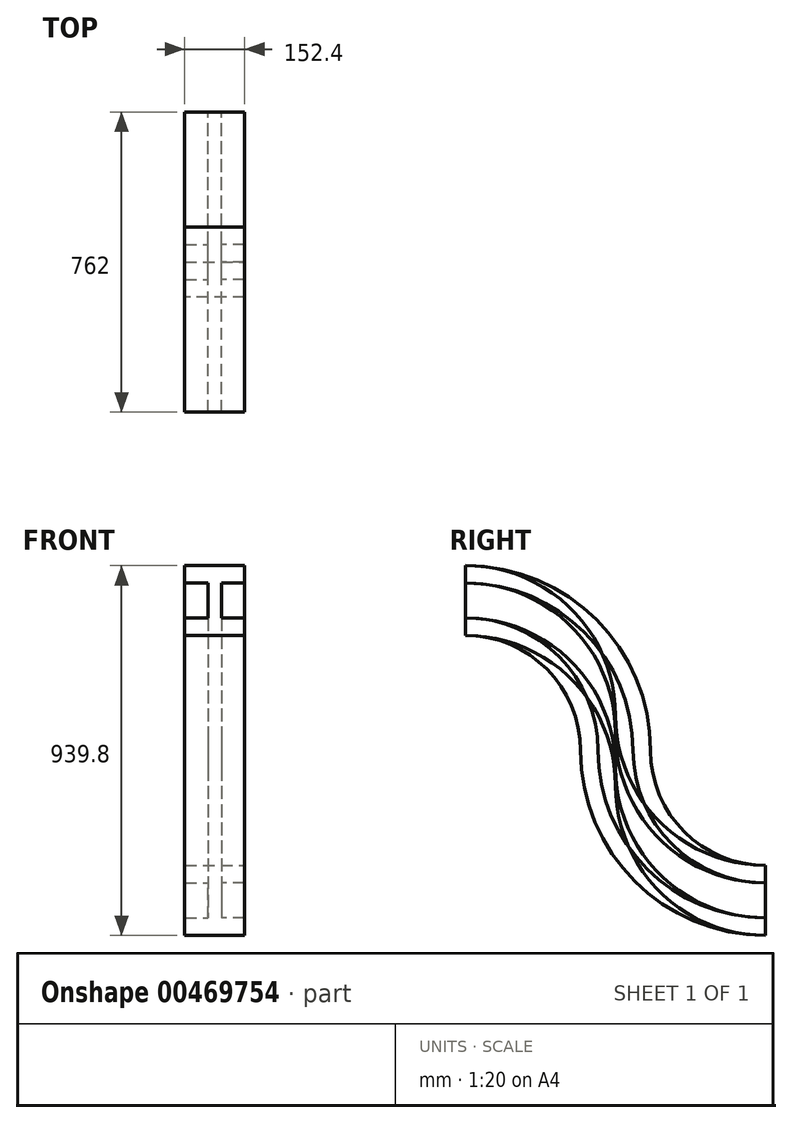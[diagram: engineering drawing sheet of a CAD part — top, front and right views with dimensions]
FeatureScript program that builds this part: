
annotation { "Feature Type Name" : "Feature", "Feature Type Description" : "" }
export const myFeature = defineFeature(function(context is Context, id is Id, definition is map)
    precondition{}
    {
        {
            var Q0;
            Q0=qCreatedBy(makeId("Front.planeOp"),FACE);
            var sketch = newSketch(context, id + "F0", { "sketchPlane" : qUnion([Q0])});
            skLineSegment(sketch, "E0", {"start": v(0, 88.9) * mm, "end": v(76.2, 88.9) * mm});
            skLineSegment(sketch, "E1", {"start": v(76.2, 88.9) * mm, "end": v(76.2, 44.45) * mm});
            skLineSegment(sketch, "E2", {"start": v(76.2, 44.45) * mm, "end": v(17.37, 44.45) * mm});
            skLineSegment(sketch, "E3", {"start": v(0, 88.9) * mm, "end": v(0, -88.9) * mm, "construction": true});
            skLineSegment(sketch, "E4", {"start": v(-17.37, 0) * mm, "end": v(17.37, 0) * mm, "construction": true});
            skLineSegment(sketch, "E5", {"start": v(17.37, 0) * mm, "end": v(17.37, 44.45) * mm});
            skLineSegment(sketch, "E6.MirrorCS", {"start": v(0, 88.9) * mm, "end": v(-76.2, 88.9) * mm});
            skLineSegment(sketch, "E7.MirrorCS", {"start": v(-76.2, 88.9) * mm, "end": v(-76.2, 44.45) * mm});
            skLineSegment(sketch, "E8.MirrorCS", {"start": v(-17.37, 0) * mm, "end": v(-17.37, 44.45) * mm});
            skLineSegment(sketch, "E9.MirrorCS", {"start": v(-76.2, 44.45) * mm, "end": v(-17.37, 44.45) * mm});
            skLineSegment(sketch, "E10.MirrorCS", {"start": v(0, -88.9) * mm, "end": v(-76.2, -88.9) * mm});
            skLineSegment(sketch, "E11.MirrorCS", {"start": v(-76.2, -88.9) * mm, "end": v(-76.2, -44.45) * mm});
            skLineSegment(sketch, "E12.MirrorCS", {"start": v(-76.2, -44.45) * mm, "end": v(-17.37, -44.45) * mm});
            skLineSegment(sketch, "E13.MirrorCS", {"start": v(-17.37, 0) * mm, "end": v(-17.37, -44.45) * mm});
            skLineSegment(sketch, "E14.MirrorCS", {"start": v(76.2, -44.45) * mm, "end": v(17.37, -44.45) * mm});
            skLineSegment(sketch, "E15.MirrorCS", {"start": v(0, -88.9) * mm, "end": v(76.2, -88.9) * mm});
            skLineSegment(sketch, "E16.MirrorCS", {"start": v(17.37, 0) * mm, "end": v(17.37, -44.45) * mm});
            skLineSegment(sketch, "E17.MirrorCS", {"start": v(76.2, -88.9) * mm, "end": v(76.2, -44.45) * mm});
            skSolve(sketch);
        }
        {
            var Q0;
            Q0=qCreatedBy(makeId("Right.planeOp"),FACE);
            var sketch = newSketch(context, id + "F1", { "sketchPlane" : qUnion([Q0])});
            skArc(sketch, "E18", {"start": v(0, 0) * mm, "mid": v(269.4, -111.6) * mm, "end": v(381, -381) * mm});
            skArc(sketch, "E19", {"start": v(381, -381) * mm, "mid": v(492.6, -650.4) * mm, "end": v(762, -762) * mm});
            skSolve(sketch);
        }
        {
            var Q0;
            Q0=makeQuery(id+"F0.imprint","IMPRINT",FACE,{"disambiguationData":[TD([[makeQuery(id+"F0.imprint","IMPRINT",EDGE,{"derivedFrom":sQuery(id+"F0.wireOp",EDGE,"E0")}),-1.0]])]});
            var Q1;
            Q1=sQuery(id+"F1.wireOp",EDGE,"E18");
            var Q2;
            Q2=sQuery(id+"F1.wireOp",EDGE,"E19");
            sweep(context, id + "F2", {"profiles" : qUnion([Q0]), "path" : qUnion([Q1, Q2]), "keepProfileOrientation" : true});
        }
        {
            var Q0;
            Q0=makeQuery(id+"F0.imprint","IMPRINT",FACE,{"disambiguationData":[TD([[makeQuery(id+"F0.imprint","IMPRINT",EDGE,{"derivedFrom":sQuery(id+"F0.wireOp",EDGE,"E0")}),-1.0]])]});
            var Q1;
            Q1=sQuery(id+"F1.wireOp",EDGE,"E18");
            var Q2;
            Q2=sQuery(id+"F1.wireOp",EDGE,"E19");
            sweep(context, id + "F3", {"profiles" : qUnion([Q0]), "path" : qUnion([Q1, Q2])});
        }
    });
